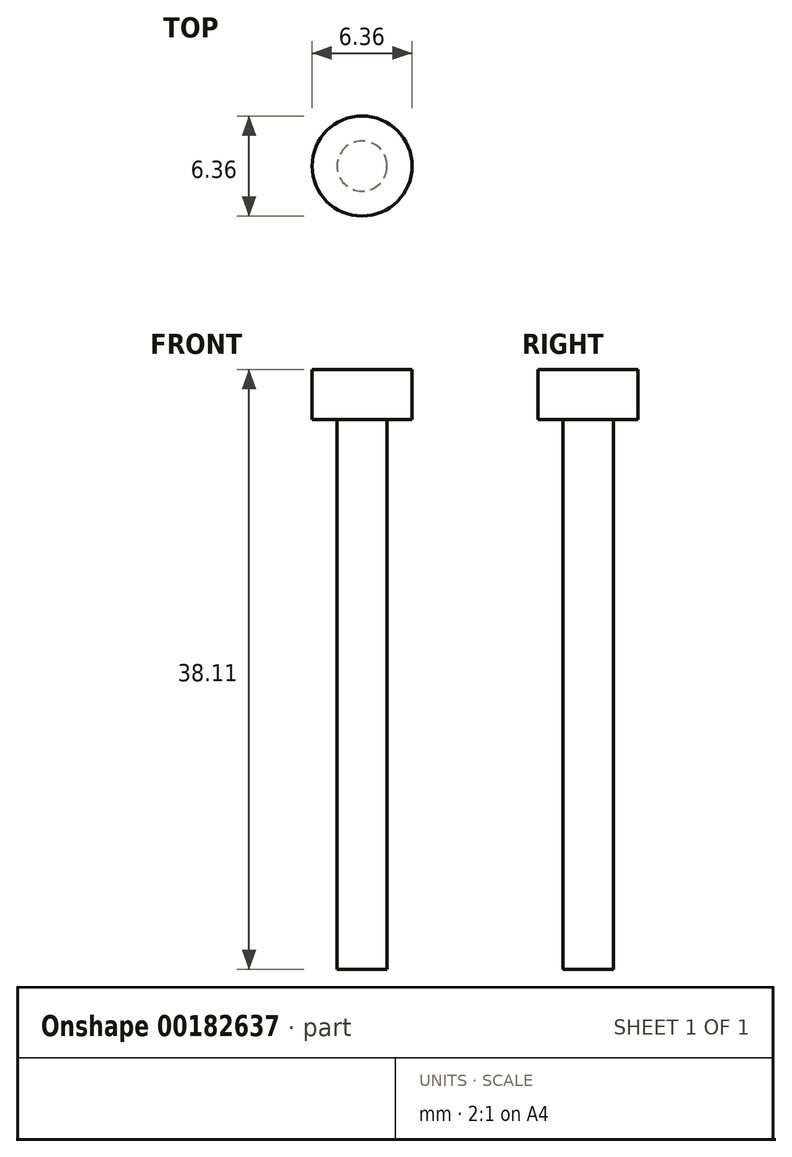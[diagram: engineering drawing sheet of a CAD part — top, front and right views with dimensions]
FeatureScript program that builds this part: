
annotation { "Feature Type Name" : "Feature", "Feature Type Description" : "" }
export const myFeature = defineFeature(function(context is Context, id is Id, definition is map)
    precondition{}
    {
        {
            var Q0;
            Q0=qCreatedBy(makeId("Top.planeOp"),FACE);
            var sketch = newSketch(context, id + "F0", { "sketchPlane" : qUnion([Q0])});
            skCircle(sketch, "E0", {"center": v(0, 0) * mm, "radius": 3.18 * mm});
            skSolve(sketch);
        }
        {
            var Q0;
            Q0=makeQuery(id+"F0.imprint","IMPRINT",FACE,{"disambiguationData":[TD([[makeQuery(id+"F0.imprint","IMPRINT",EDGE,{"derivedFrom":sQuery(id+"F0.wireOp",EDGE,"E0")}),1.0]])]});
            extrude(context, id + "F1", {"entities" : qUnion([Q0]), "depth" : 3.17 * mm});
        }
        {
            var Q0;
            Q0=makeQuery(id+"F1.opExtrude","CAP_FACE",FACE,{"disambiguationData":[OSD([sQuery(id+"F0.wireOp",EDGE,"E0")])],"isStart":false});
            var sketch = newSketch(context, id + "F2", { "sketchPlane" : qUnion([Q0])});
            skCircle(sketch, "E1.cCircle", {"center": v(0, 0) * mm, "radius": 1.37 * mm, "construction": true});
            skLineSegment(sketch, "E1.0", {"start": v(0.2, 1.58) * mm, "end": v(1.46, 0.62) * mm});
            skLineSegment(sketch, "E1.1", {"start": v(1.46, 0.62) * mm, "end": v(1.27, -0.95) * mm});
            skLineSegment(sketch, "E1.2", {"start": v(1.27, -0.95) * mm, "end": v(-0.2, -1.58) * mm});
            skLineSegment(sketch, "E1.3", {"start": v(-0.2, -1.58) * mm, "end": v(-1.46, -0.62) * mm});
            skLineSegment(sketch, "E1.4", {"start": v(-1.46, -0.62) * mm, "end": v(-1.27, 0.95) * mm});
            skLineSegment(sketch, "E1.5", {"start": v(-1.27, 0.95) * mm, "end": v(0.2, 1.58) * mm});
            skPoint(sketch, "E1.0.midPoint", {"position": v(0.83, 1.1) * mm});
            skSolve(sketch);
        }
        {
            var Q0;
            Q0=makeQuery(id+"F1.opExtrude","CAP_FACE",FACE,{"disambiguationData":[OSD([sQuery(id+"F0.wireOp",EDGE,"E0")])],"isStart":true});
            var sketch = newSketch(context, id + "F3", { "sketchPlane" : qUnion([Q0])});
            skCircle(sketch, "E2", {"center": v(0, 0) * mm, "radius": 1.6 * mm});
            skSolve(sketch);
        }
        {
            var Q0;
            Q0=makeQuery(id+"F3.imprint","IMPRINT",FACE,{"disambiguationData":[TD([[makeQuery(id+"F3.imprint","IMPRINT",EDGE,{"derivedFrom":sQuery(id+"F3.wireOp",EDGE,"E2")}),1.0]])]});
            extrude(context, id + "F4", {"entities" : qUnion([Q0]), "operationType" : NewBodyOperationType.ADD, "depth" : 34.92 * mm});
        }
    });
